# Revit family: ROTHOB_Rothoblaas_Screw_VGSPlate
name_source: partatom
category: Structural Connections
units: mm (PartAtom-declared; Revit-internal decimal feet)

## family parameters
Cut with Voids When Loaded = No
Enable cutting in views = Yes
Host = Face
Material for Model Behavior = Steel
OmniClass Number = 23.20.40.11.14.24
OmniClass Title = Screws
Shared = No

## types (10) — shared parameters
AssetType = Fixed
AssociatedDensity_ρa_BeechLVLPredrilled = 730.00 kg/m³
AssociatedDensity_ρa_LVLSoftwood = 500.00 kg/m³
AssociatedDensity_ρa_Softwood = 350.00 kg/m³
AtmosphericCorrosivity = C1 | C2
BIMObjectName = ROTHOB_Rothoblaas_Screw_VGSPlate
CECode = ETA-11/0030
CETitle = Rotho Blaas Self-tapping screws and threaded rods
CalculationDensity_ρk_BeechLVLPredrilled = 590 ÷ 750 kg/m³
CalculationDensity_ρk_LVLSoftwood = 460 ÷ 550 kg/m³
CalculationDensity_ρk_Softwood = ≤ 440 kg/m³
Category = Pr_20_29_76_75: Self-tapping screws
CodePerformance = CE - Construction products
Color = Black
Default Elevation = 1219.2 mm  [stored 4 ft]
Description = Pan Head Hexagonal Screw for lifting
DurationUnit = Years
Esporta tipo in formato IFC con nome = IfcMechanicalFastenerType
ExpectedLife = 50
Features = Full-threaded screw for lifting or steel-timber connection
Finish = Black zinc plated
HeadDiameterS_dks = 16.5 mm  [stored 0.0541339 ft]
HeadDiameter_dk = 20 mm  [stored 0.0656168 ft]
HeadThickness_t1 = 16.25 mm  [stored 0.0533136 ft]
HeadWasherThickness_twt = 2.5 mm  [stored 0.0082021 ft]
HexagonalHeadThickness_ts = 5.75 mm  [stored 0.0188648 ft]
HoleDiameterOnSteelPlate_dvs = 13 mm
IfcExportAs = IfcMechanicalFastenerType
IfcExportType = USERDEFINED
ManufacturerName = ROTHO BLAAS SRL
ManufacturerURL = www.rothoblaas.com
Material = Electrogalvanized carbon steel
ModelDisclaimer = The latest version of the data sheets can be found on our website
Name = Screw
NominalDiameter = 11 mm  [stored 0.0360892 ft]
NominalDiameter_d1 = 11 mm  [stored 0.0360892 ft]
ObjectMaterial = ROTHOB_Rothoblaas_CarbonSteel_Electrogalvanized_Black
OmniClassCode = 23.20.40.11.14.24
OmniClassTitle = Screws
OmniClassVersion = 2012-05-16
PredrillingHoleDiameterHardwood_dvh = 7 mm  [stored 0.0229659 ft]
PredrillingHoleDiameterSoftwood_dvs = 6 mm  [stored 0.019685 ft]
ProductInformation = www.rothoblaas.com/products/fastening/screws/vgs-plate
Revision = 000
ServiceClass = SC1 | SC2
Shape = Cylindrical
TensileStrength_ftens,k = 38.00 kN
ThreadDiameter_d2 = 6.6 mm  [stored 0.0216535 ft]
TipLength_Lt = 13.2 mm  [stored 0.0433071 ft]
Tipo IFC predefinito = USERDEFINED
UnderheadDiameter_duk = 12 mm  [stored 0.0393701 ft]
UnderheadLength_L1 = 3 mm  [stored 0.00984252 ft]
UniClass2015Code = Pr_20_29_76_75
UniClass2015Title = Self-tapping screws
UniClass2015Version = Products v1.41
Version = 001
WithdrawalResistance_BeechLVLPredrilled = 29.000 N/mm²
WithdrawalResistance_LVLSoftwood = 15.000 N/mm²
WithdrawalResistance_Softwood = 11.700 N/mm²
WoodCorrosivity = T1 | T2
WrenchSize_SW = 17 mm
YieldMoment_My,k = 45.90 N-m

## per-type parameters (varying)
| type | GTIN | ICC-ESCode | ICC-ESTitle | InsertionLength_L | MinWeight | ModelNumber | ModelNumberCode | NominalLength | Size | ThreadLength_b |
| VGSPL1160_11x60mm | 8055598651785 |  |  | 60 mm  [stored 0.19685 ft] | 0.034 kg | VGSPL1160 | 1160 | 60 mm  [stored 0.19685 ft] | 11x60 mm | 50 mm  [stored 0.164042 ft] |
| VGSPL1180_11x80mm | 8055598651808 | ESR-4645 / ELC-4645 | Rotho blaas self-tapping wood screws / Rotho Blaas Self-tapping Wood Screws | 80 mm  [stored 0.262467 ft] | 0.042 kg | VGSPL1180 | 1180 | 80 mm  [stored 0.262467 ft] | 11x80 mm | 70 mm  [stored 0.229659 ft] |
| VGSPL11100_11x100mm | 8055598651839 | ESR-4645 / ELC-4645 | Rotho blaas self-tapping wood screws / Rotho Blaas Self-tapping Wood Screws | 100 mm  [stored 0.328084 ft] | 0.050 kg | VGSPL11100 | 11100 | 100 mm  [stored 0.328084 ft] | 11x100 mm | 90 mm  [stored 0.295276 ft] |
| VGSPL11120_11x120mm | 8055598651747 | ESR-4645 / ELC-4645 | Rotho blaas self-tapping wood screws / Rotho Blaas Self-tapping Wood Screws | 120 mm  [stored 0.393701 ft] | 0.057 kg | VGSPL11120 | 11120 | 120 mm  [stored 0.393701 ft] | 11x120 mm | 110 mm  [stored 0.360892 ft] |
| VGSPL11140_11x140mm | 8055598651754 | ESR-4645 / ELC-4645 | Rotho blaas self-tapping wood screws / Rotho Blaas Self-tapping Wood Screws | 140 mm  [stored 0.459318 ft] | 0.065 kg | VGSPL11140 | 11140 | 140 mm  [stored 0.459318 ft] | 11x140 mm | 130 mm  [stored 0.426509 ft] |
| VGSPL11160_11x160mm | 8055598651822 | ESR-4645 / ELC-4645 | Rotho blaas self-tapping wood screws / Rotho Blaas Self-tapping Wood Screws | 160 mm  [stored 0.524934 ft] | 0.072 kg | VGSPL11160 | 11160 | 160 mm  [stored 0.524934 ft] | 11x160 mm | 150 mm |
| VGSPL11180_11x180mm | 8055598651815 | ESR-4645 / ELC-4645 | Rotho blaas self-tapping wood screws / Rotho Blaas Self-tapping Wood Screws | 180 mm  [stored 0.590551 ft] | 0.080 kg | VGSPL11180 | 11180 | 180 mm  [stored 0.590551 ft] | 11x180 mm | 170 mm  [stored 0.557743 ft] |
| VGSPL11200_11x200mm | 8055598651778 | ESR-4645 / ELC-4645 | Rotho blaas self-tapping wood screws / Rotho Blaas Self-tapping Wood Screws | 200 mm  [stored 0.656168 ft] | 0.088 kg | VGSPL11200 | 11200 | 200 mm  [stored 0.656168 ft] | 11x200 mm | 190 mm |
| VGSPL11240_11x240mm | 8055598651792 | ESR-4645 / ELC-4645 | Rotho blaas self-tapping wood screws / Rotho Blaas Self-tapping Wood Screws | 240 mm  [stored 0.787402 ft] | 0.103 kg | VGSPL11240 | 11240 | 240 mm  [stored 0.787402 ft] | 11x240 mm | 230 mm  [stored 0.754593 ft] |
| VGSPL11280_11x280mm | 8055598651761 | ESR-4645 / ELC-4645 | Rotho blaas self-tapping wood screws / Rotho Blaas Self-tapping Wood Screws | 280 mm  [stored 0.918635 ft] | 0.118 kg | VGSPL11280 | 11280 | 280 mm  [stored 0.918635 ft] | 11x280 mm | 270 mm  [stored 0.885827 ft] |

note: [stored X ft] marks values corroborated as IEEE doubles in the binary element streams (Revit-internal decimal feet)
